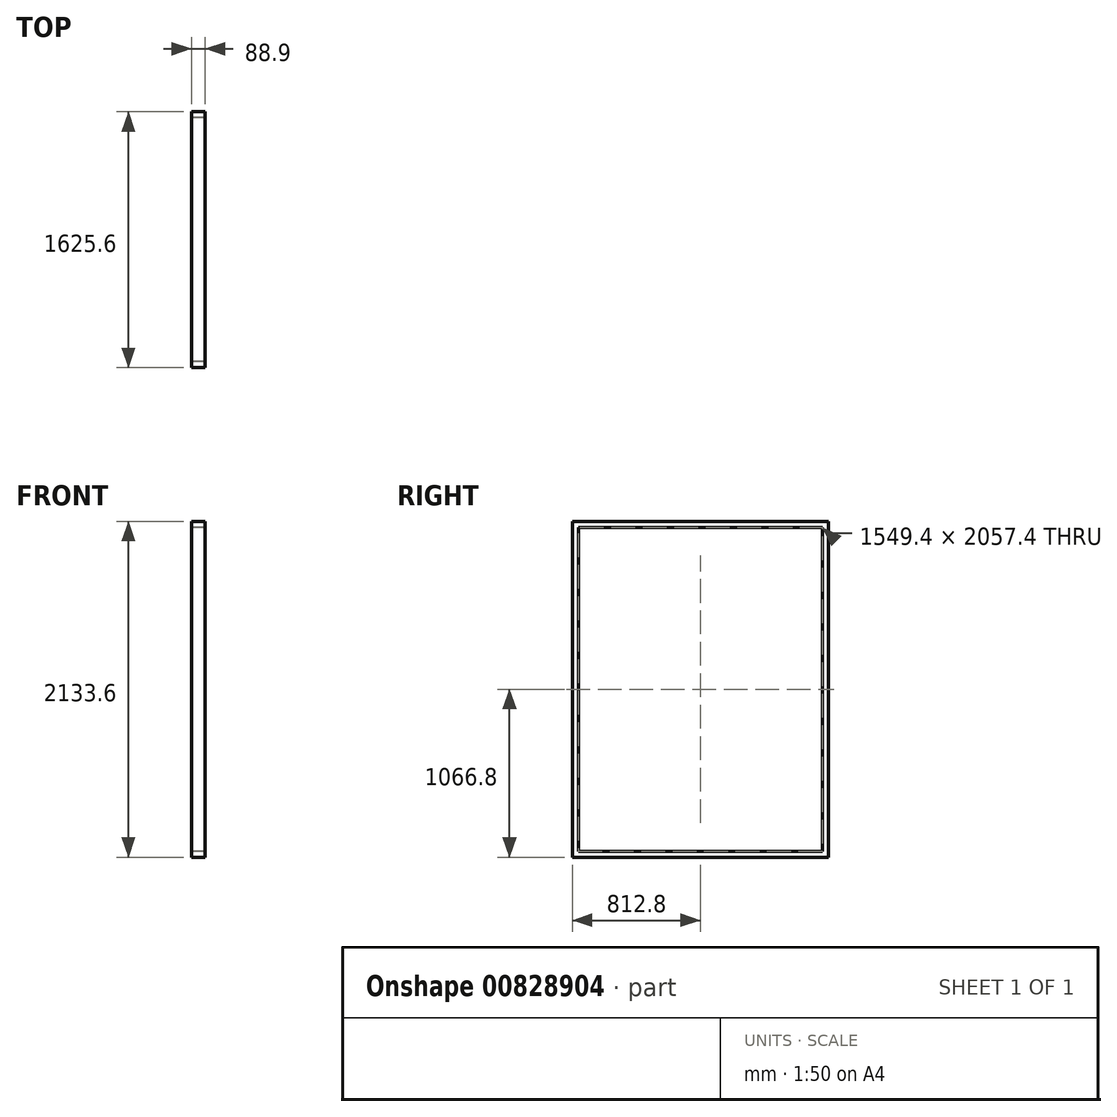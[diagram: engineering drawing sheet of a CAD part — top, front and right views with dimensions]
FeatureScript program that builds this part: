
annotation { "Feature Type Name" : "Feature", "Feature Type Description" : "" }
export const myFeature = defineFeature(function(context is Context, id is Id, definition is map)
    precondition{}
    {
        {
            var Q0;
            Q0=qCreatedBy(makeId("Right.planeOp"),FACE);
            var sketch = newSketch(context, id + "F0", { "sketchPlane" : qUnion([Q0])});
            skLineSegment(sketch, "E0.bottom", {"start": v(-839.98, -1049.2) * mm, "end": v(785.62, -1049.2) * mm});
            skLineSegment(sketch, "E0.top", {"start": v(-839.98, -1011.1) * mm, "end": v(785.62, -1011.1) * mm});
            skLineSegment(sketch, "E0.left", {"start": v(-839.98, -1049.2) * mm, "end": v(-839.98, -1011.1) * mm});
            skLineSegment(sketch, "E0.right", {"start": v(785.62, -1049.2) * mm, "end": v(785.62, -1011.1) * mm});
            skLineSegment(sketch, "E1.bottom", {"start": v(785.62, -1011.1) * mm, "end": v(747.52, -1011.1) * mm});
            skLineSegment(sketch, "E1.top", {"start": v(785.62, 1046.3) * mm, "end": v(747.52, 1046.3) * mm});
            skLineSegment(sketch, "E1.left", {"start": v(785.62, -1011.1) * mm, "end": v(785.62, 1046.3) * mm});
            skLineSegment(sketch, "E1.right", {"start": v(747.52, -1011.1) * mm, "end": v(747.52, 1046.3) * mm});
            skLineSegment(sketch, "E2.bottom", {"start": v(-839.98, -1011.1) * mm, "end": v(-801.88, -1011.1) * mm});
            skLineSegment(sketch, "E2.top", {"start": v(-839.98, 1046.3) * mm, "end": v(-801.88, 1046.3) * mm});
            skLineSegment(sketch, "E2.left", {"start": v(-839.98, -1011.1) * mm, "end": v(-839.98, 1046.3) * mm});
            skLineSegment(sketch, "E2.right", {"start": v(-801.88, -1011.1) * mm, "end": v(-801.88, 1046.3) * mm});
            skLineSegment(sketch, "E3", {"start": v(-801.88, -1011.1) * mm, "end": v(-433.58, -1011.1) * mm, "construction": true});
            skLineSegment(sketch, "E4.bottom", {"start": v(-433.58, -1011.1) * mm, "end": v(-395.48, -1011.1) * mm});
            skLineSegment(sketch, "E4.top", {"start": v(-433.58, 1046.3) * mm, "end": v(-395.48, 1046.3) * mm});
            skLineSegment(sketch, "E4.left", {"start": v(-433.58, -1011.1) * mm, "end": v(-433.58, 1046.3) * mm});
            skLineSegment(sketch, "E4.right", {"start": v(-395.48, -1011.1) * mm, "end": v(-395.48, 1046.3) * mm});
            skLineSegment(sketch, "E5", {"start": v(-395.48, -1011.1) * mm, "end": v(-27.18, -1011.1) * mm, "construction": true});
            skLineSegment(sketch, "E6.bottom", {"start": v(-27.18, -1011.1) * mm, "end": v(10.92, -1011.1) * mm});
            skLineSegment(sketch, "E6.top", {"start": v(-27.18, 1046.3) * mm, "end": v(10.92, 1046.3) * mm});
            skLineSegment(sketch, "E6.left", {"start": v(-27.18, -1011.1) * mm, "end": v(-27.18, 1046.3) * mm});
            skLineSegment(sketch, "E6.right", {"start": v(10.92, -1011.1) * mm, "end": v(10.92, 1046.3) * mm});
            skLineSegment(sketch, "E7", {"start": v(10.92, -1011.1) * mm, "end": v(379.22, -1011.1) * mm, "construction": true});
            skLineSegment(sketch, "E8.bottom", {"start": v(379.22, -1011.1) * mm, "end": v(417.32, -1011.1) * mm});
            skLineSegment(sketch, "E8.top", {"start": v(379.22, 1046.3) * mm, "end": v(417.32, 1046.3) * mm});
            skLineSegment(sketch, "E8.left", {"start": v(379.22, -1011.1) * mm, "end": v(379.22, 1046.3) * mm});
            skLineSegment(sketch, "E8.right", {"start": v(417.32, -1011.1) * mm, "end": v(417.32, 1046.3) * mm});
            skLineSegment(sketch, "E9", {"start": v(417.32, -1011.1) * mm, "end": v(747.52, -1011.1) * mm, "construction": true});
            skLineSegment(sketch, "E10.bottom", {"start": v(-839.98, 1046.3) * mm, "end": v(785.62, 1046.3) * mm});
            skLineSegment(sketch, "E10.top", {"start": v(-839.98, 1084.4) * mm, "end": v(785.62, 1084.4) * mm});
            skLineSegment(sketch, "E10.left", {"start": v(-839.98, 1046.3) * mm, "end": v(-839.98, 1084.4) * mm});
            skLineSegment(sketch, "E10.right", {"start": v(785.62, 1046.3) * mm, "end": v(785.62, 1084.4) * mm});
            skSolve(sketch);
        }
        {
            var Q0;
            Q0 = qSketchRegion(id + "F0", true);
            var Q1;
            Q1=makeQuery(id+"F0.imprint","IMPRINT",FACE,{"disambiguationData":[TD([[makeQuery(id+"F0.imprint","IMPRINT",EDGE,{"derivedFrom":sQuery(id+"F0.wireOp",EDGE,"E4.bottom")}),1.0]])]});
            var Q2;
            Q2=makeQuery(id+"F0.imprint","IMPRINT",FACE,{"disambiguationData":[TD([[makeQuery(id+"F0.imprint","IMPRINT",EDGE,{"derivedFrom":sQuery(id+"F0.wireOp",EDGE,"E6.bottom")}),1.0]])]});
            var Q3;
            Q3=makeQuery(id+"F0.imprint","IMPRINT",FACE,{"disambiguationData":[TD([[makeQuery(id+"F0.imprint","IMPRINT",EDGE,{"derivedFrom":sQuery(id+"F0.wireOp",EDGE,"E8.bottom")}),1.0]])]});
            extrude(context, id + "F1", {"entities" : qUnion([Q0, Q1, Q2, Q3]), "depth" : 88.9 * mm, "offsetDistance" : 25.4 * mm});
        }
    });
